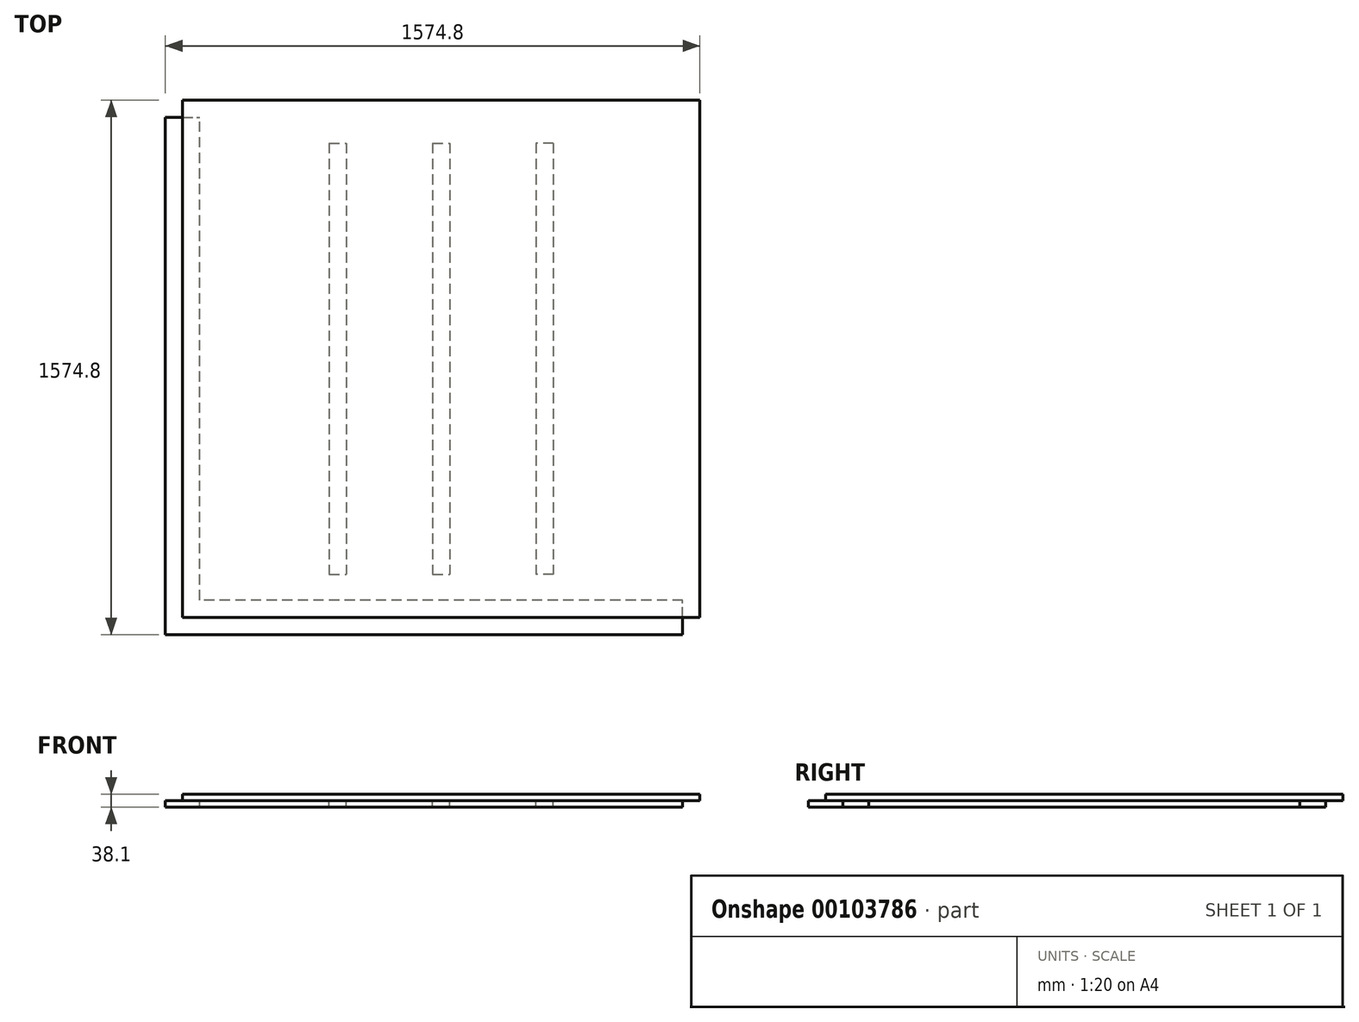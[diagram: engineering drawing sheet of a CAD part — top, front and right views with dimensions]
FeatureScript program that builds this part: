
annotation { "Feature Type Name" : "Feature", "Feature Type Description" : "" }
export const myFeature = defineFeature(function(context is Context, id is Id, definition is map)
    precondition{}
    {
        {
            var Q0;
            Q0=qCreatedBy(makeId("Top.planeOp"),FACE);
            var sketch = newSketch(context, id + "F0", { "sketchPlane" : qUnion([Q0])});
            skLineSegment(sketch, "E0.bottom", {"start": v(762, -762) * mm, "end": v(-762, -762) * mm});
            skLineSegment(sketch, "E0.top", {"start": v(762, 762) * mm, "end": v(-762, 762) * mm});
            skLineSegment(sketch, "E0.left", {"start": v(762, -762) * mm, "end": v(762, 762) * mm});
            skLineSegment(sketch, "E0.right", {"start": v(-762, -762) * mm, "end": v(-762, 762) * mm});
            skPoint(sketch, "E0.middle", {"position": v(0, 0) * mm});
            skSolve(sketch);
        }
        {
            var Q0;
            Q0 = qSketchRegion(id + "F0", true);
            extrude(context, id + "F1", {"entities" : qUnion([Q0]), "depth" : 19.05 * mm});
        }
        {
            var Q0;
            Q0=makeQuery(id+"F1.opExtrude","CAP_FACE",FACE,{"disambiguationData":[OSD([sQuery(id+"F0.wireOp",EDGE,"E0.bottom"),sQuery(id+"F0.wireOp",EDGE,"E0.top"),sQuery(id+"F0.wireOp",EDGE,"E0.left"),sQuery(id+"F0.wireOp",EDGE,"E0.right")])],"isStart":true});
            var sketch = newSketch(context, id + "F2", { "sketchPlane" : qUnion([Q0])});
            skLineSegment(sketch, "E1.bottom", {"start": v(-711.2, 762) * mm, "end": v(-812.8, 762) * mm, "construction": true});
            skLineSegment(sketch, "E1.top", {"start": v(-711.2, -762) * mm, "end": v(-812.8, -762) * mm, "construction": true});
            skLineSegment(sketch, "E1.left", {"start": v(-711.2, 762) * mm, "end": v(-711.2, 711.2) * mm, "construction": true});
            skLineSegment(sketch, "E1.right", {"start": v(-812.8, 762) * mm, "end": v(-812.8, -711.2) * mm});
            skLineSegment(sketch, "E2.bottom", {"start": v(762, 711.2) * mm, "end": v(711.2, 711.2) * mm, "construction": true});
            skLineSegment(sketch, "E2.top", {"start": v(762, 812.8) * mm, "end": v(711.2, 812.8) * mm, "construction": true});
            skLineSegment(sketch, "E2.left", {"start": v(762, 711.2) * mm, "end": v(762, 812.8) * mm, "construction": true});
            skLineSegment(sketch, "E2.right", {"start": v(-812.8, 711.2) * mm, "end": v(-812.8, 812.8) * mm});
            skLineSegment(sketch, "E3", {"start": v(-711.2, 711.2) * mm, "end": v(-812.8, 711.2) * mm, "construction": true});
            skLineSegment(sketch, "E4", {"start": v(-711.2, 711.2) * mm, "end": v(-711.2, -711.2) * mm});
            skLineSegment(sketch, "E5", {"start": v(711.2, 812.8) * mm, "end": v(711.2, 711.2) * mm});
            skLineSegment(sketch, "E6", {"start": v(-812.8, -711.2) * mm, "end": v(-711.2, -711.2) * mm});
            skLineSegment(sketch, "E7", {"start": v(-812.8, -711.2) * mm, "end": v(-812.8, -762) * mm, "construction": true});
            skLineSegment(sketch, "E8", {"start": v(-711.2, -711.2) * mm, "end": v(-711.2, -762) * mm, "construction": true});
            skLineSegment(sketch, "E9", {"start": v(711.2, 812.8) * mm, "end": v(-812.8, 812.8) * mm});
            skLineSegment(sketch, "E10", {"start": v(711.2, 711.2) * mm, "end": v(-711.2, 711.2) * mm});
            skSolve(sketch);
        }
        {
            var Q0;
            Q0 = qSketchRegion(id + "F2", true);
            extrude(context, id + "F3", {"entities" : qUnion([Q0]), "depth" : 19.05 * mm});
        }
        {
            var Q0;
            Q0=makeQuery(id+"F1.opExtrude","CAP_FACE",FACE,{"disambiguationData":[OSD([sQuery(id+"F0.wireOp",EDGE,"E0.bottom"),sQuery(id+"F0.wireOp",EDGE,"E0.top"),sQuery(id+"F0.wireOp",EDGE,"E0.left"),sQuery(id+"F0.wireOp",EDGE,"E0.right")])],"isStart":true});
            var sketch = newSketch(context, id + "F4", { "sketchPlane" : qUnion([Q0])});
            skLineSegment(sketch, "E11.bottom", {"start": v(-25.4, -635) * mm, "end": v(25.4, -635) * mm});
            skLineSegment(sketch, "E11.top", {"start": v(-25.4, 635) * mm, "end": v(25.4, 635) * mm});
            skLineSegment(sketch, "E11.left", {"start": v(-25.4, -635) * mm, "end": v(-25.4, 635) * mm});
            skLineSegment(sketch, "E11.right", {"start": v(25.4, -635) * mm, "end": v(25.4, 635) * mm});
            skPoint(sketch, "E11.middle", {"position": v(0, 0) * mm});
            skLineSegment(sketch, "E12.bottom", {"start": v(-330.2, -635) * mm, "end": v(-279.4, -635) * mm});
            skLineSegment(sketch, "E12.top", {"start": v(-330.2, 635) * mm, "end": v(-279.4, 635) * mm});
            skLineSegment(sketch, "E12.left", {"start": v(-330.2, -635) * mm, "end": v(-330.2, 635) * mm});
            skLineSegment(sketch, "E12.right", {"start": v(-279.4, -635) * mm, "end": v(-279.4, 635) * mm});
            skPoint(sketch, "E12.middle", {"position": v(-304.8, 0) * mm});
            skLineSegment(sketch, "E13", {"start": v(0, 0) * mm, "end": v(-304.8, 0) * mm, "construction": true});
            skPoint(sketch, "E13.endSnap0", {"position": v(-25.4, 0) * mm});
            skLineSegment(sketch, "E14", {"start": v(0, 0) * mm, "end": v(304.8, 0) * mm, "construction": true});
            skLineSegment(sketch, "E15.bottom", {"start": v(330.2, -635) * mm, "end": v(279.4, -635) * mm});
            skLineSegment(sketch, "E15.top", {"start": v(330.2, 635) * mm, "end": v(279.4, 635) * mm});
            skLineSegment(sketch, "E15.left", {"start": v(330.2, -635) * mm, "end": v(330.2, 635) * mm});
            skLineSegment(sketch, "E15.right", {"start": v(279.4, -635) * mm, "end": v(279.4, 635) * mm});
            skPoint(sketch, "E15.middle", {"position": v(304.8, 0) * mm});
            skSolve(sketch);
        }
        {
            var Q0;
            Q0 = qSketchRegion(id + "F4", true);
            extrude(context, id + "F5", {"entities" : qUnion([Q0]), "depth" : 19.05 * mm});
        }
    });
